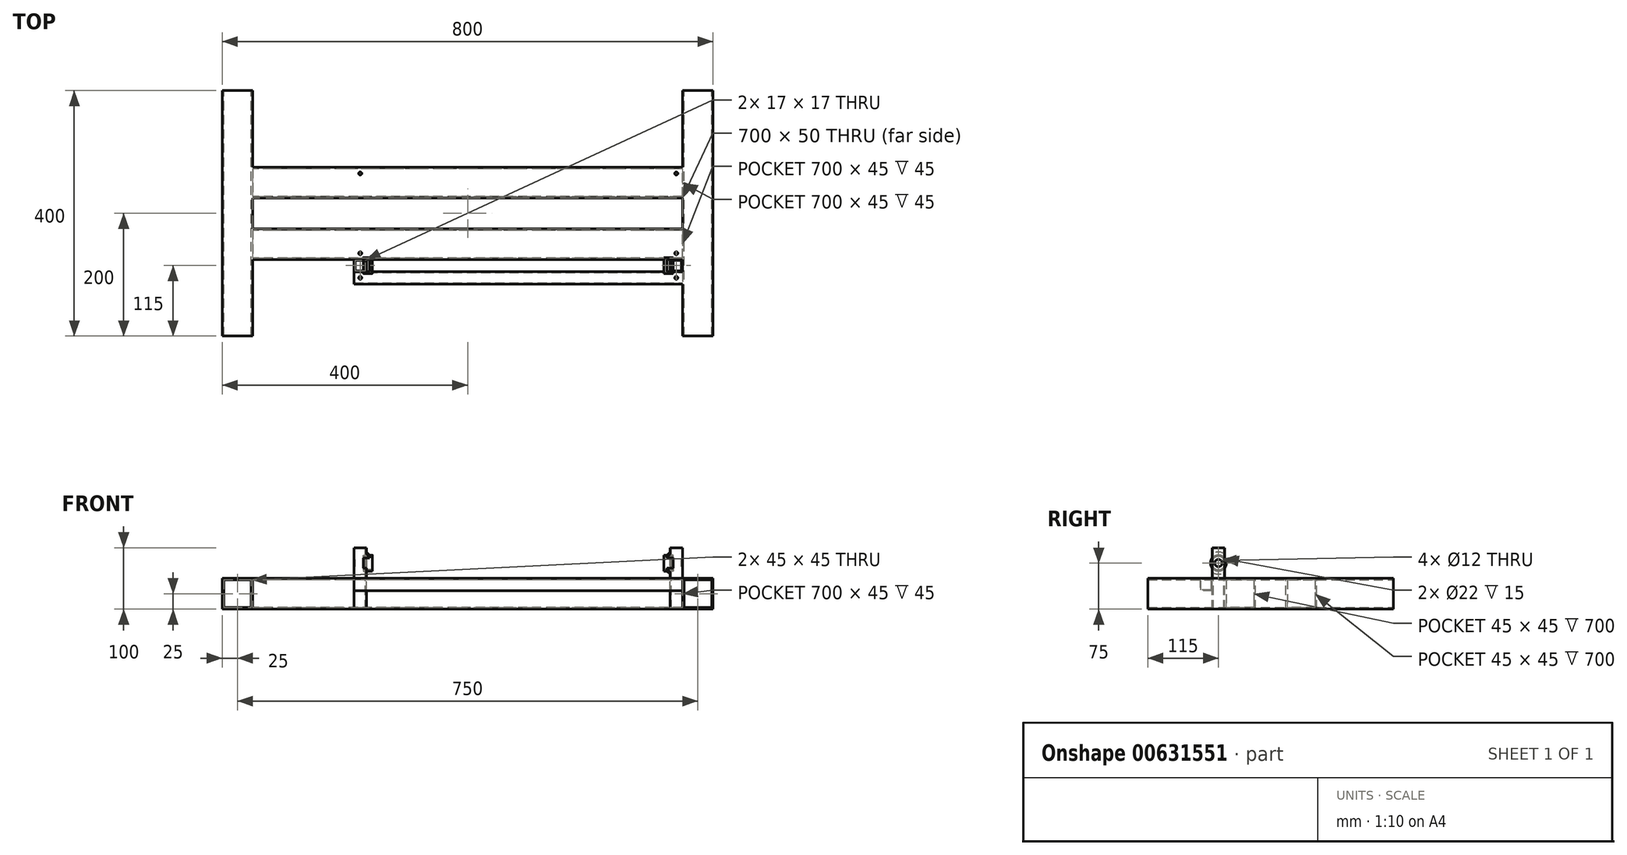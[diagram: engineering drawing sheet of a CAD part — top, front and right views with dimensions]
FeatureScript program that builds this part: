
annotation { "Feature Type Name" : "Feature", "Feature Type Description" : "" }
export const myFeature = defineFeature(function(context is Context, id is Id, definition is map)
    precondition{}
    {
        {
            var Q0;
            Q0=qCreatedBy(makeId("Front.planeOp"),FACE);
            var sketch = newSketch(context, id + "F0", { "sketchPlane" : qUnion([Q0])});
            skLineSegment(sketch, "E0.bottom", {"start": v(-400, -25) * mm, "end": v(-350, -25) * mm});
            skLineSegment(sketch, "E0.top", {"start": v(-400, 25) * mm, "end": v(-350, 25) * mm});
            skLineSegment(sketch, "E0.left", {"start": v(-400, -25) * mm, "end": v(-400, 25) * mm});
            skLineSegment(sketch, "E0.right", {"start": v(-350, -25) * mm, "end": v(-350, 25) * mm});
            skPoint(sketch, "E0.middle", {"position": v(-375, 0) * mm});
            skLineSegment(sketch, "E1.bottom", {"start": v(350, -25) * mm, "end": v(400, -25) * mm});
            skLineSegment(sketch, "E1.top", {"start": v(350, 25) * mm, "end": v(400, 25) * mm});
            skLineSegment(sketch, "E1.left", {"start": v(350, -25) * mm, "end": v(350, 25) * mm});
            skLineSegment(sketch, "E1.right", {"start": v(400, -25) * mm, "end": v(400, 25) * mm});
            skPoint(sketch, "E1.middle", {"position": v(375, 0) * mm});
            skLineSegment(sketch, "E2.bottom", {"start": v(-397.5, -22.5) * mm, "end": v(-352.5, -22.5) * mm});
            skLineSegment(sketch, "E2.top", {"start": v(-397.5, 22.5) * mm, "end": v(-352.5, 22.5) * mm});
            skLineSegment(sketch, "E2.left", {"start": v(-397.5, -22.5) * mm, "end": v(-397.5, 22.5) * mm});
            skLineSegment(sketch, "E2.right", {"start": v(-352.5, -22.5) * mm, "end": v(-352.5, 22.5) * mm});
            skLineSegment(sketch, "E3.bottom", {"start": v(352.5, -22.5) * mm, "end": v(397.5, -22.5) * mm});
            skLineSegment(sketch, "E3.top", {"start": v(352.5, 22.5) * mm, "end": v(397.5, 22.5) * mm});
            skLineSegment(sketch, "E3.left", {"start": v(352.5, -22.5) * mm, "end": v(352.5, 22.5) * mm});
            skLineSegment(sketch, "E3.right", {"start": v(397.5, -22.5) * mm, "end": v(397.5, 22.5) * mm});
            skSolve(sketch);
        }
        {
            var Q0;
            Q0 = qSketchRegion(id + "F0", true);
            extrude(context, id + "F1", {"entities" : qUnion([Q0]), "endBound" : BoundingType.SYMMETRIC, "depth" : 400 * mm, "offsetDistance" : 25 * mm});
        }
        {
            var Q0;
            Q0=makeQuery(id+"F1.opExtrude","SWEPT_FACE",FACE,{"disambiguationData":[OSD([sQuery(id+"F0.wireOp",EDGE,"E0.right")])]});
            var sketch = newSketch(context, id + "F2", { "sketchPlane" : qUnion([Q0])});
            skPoint(sketch, "E4.middle", {"position": v(0, 0) * mm});
            skLineSegment(sketch, "E5.bottom", {"start": v(75, -25) * mm, "end": v(25, -25) * mm});
            skLineSegment(sketch, "E5.top", {"start": v(75, 25) * mm, "end": v(25, 25) * mm});
            skLineSegment(sketch, "E5.left", {"start": v(75, -25) * mm, "end": v(75, 25) * mm});
            skLineSegment(sketch, "E5.right", {"start": v(25, -25) * mm, "end": v(25, 25) * mm});
            skPoint(sketch, "E5.middle", {"position": v(50, 0) * mm});
            skLineSegment(sketch, "E6.bottom", {"start": v(-25, -25) * mm, "end": v(-75, -25) * mm});
            skLineSegment(sketch, "E6.top", {"start": v(-25, 25) * mm, "end": v(-75, 25) * mm});
            skLineSegment(sketch, "E6.left", {"start": v(-25, -25) * mm, "end": v(-25, 25) * mm});
            skLineSegment(sketch, "E6.right", {"start": v(-75, -25) * mm, "end": v(-75, 25) * mm});
            skPoint(sketch, "E6.middle", {"position": v(-50, 0) * mm});
            skLineSegment(sketch, "E7.bottom", {"start": v(72.5, 22.5) * mm, "end": v(27.5, 22.5) * mm});
            skLineSegment(sketch, "E7.top", {"start": v(72.5, -22.5) * mm, "end": v(27.5, -22.5) * mm});
            skLineSegment(sketch, "E7.left", {"start": v(72.5, 22.5) * mm, "end": v(72.5, -22.5) * mm});
            skLineSegment(sketch, "E7.right", {"start": v(27.5, 22.5) * mm, "end": v(27.5, -22.5) * mm});
            skLineSegment(sketch, "E8.bottom", {"start": v(-27.5, 22.5) * mm, "end": v(-72.5, 22.5) * mm});
            skLineSegment(sketch, "E8.top", {"start": v(-27.5, -22.5) * mm, "end": v(-72.5, -22.5) * mm});
            skLineSegment(sketch, "E8.left", {"start": v(-27.5, 22.5) * mm, "end": v(-27.5, -22.5) * mm});
            skLineSegment(sketch, "E8.right", {"start": v(-72.5, 22.5) * mm, "end": v(-72.5, -22.5) * mm});
            skSolve(sketch);
        }
        {
            var Q0;
            Q0 = qSketchRegion(id + "F2", true);
            extrude(context, id + "F3", {"entities" : qUnion([Q0]), "operationType" : NewBodyOperationType.ADD, "endBound" : BoundingType.UP_TO_NEXT, "depth" : 25 * mm, "offsetDistance" : 25 * mm});
        }
        {
            var Q0;
            Q0=makeQuery(id+"F3.boolean.opBoolean","MERGE",FACE,{"derivedFrom":[makeQuery(id+"F1.opExtrude","SWEPT_FACE",FACE,{"disambiguationData":[OSD([sQuery(id+"F0.wireOp",EDGE,"E0.top")])]}),makeQuery(id+"F1.opExtrude","SWEPT_FACE",FACE,{"disambiguationData":[OSD([sQuery(id+"F0.wireOp",EDGE,"E1.top")])]}),makeQuery(id+"F3.opExtrude","SWEPT_FACE",FACE,{"disambiguationData":[OSD([sQuery(id+"F2.wireOp",EDGE,"E5.top")])]}),makeQuery(id+"F3.opExtrude","SWEPT_FACE",FACE,{"disambiguationData":[OSD([sQuery(id+"F2.wireOp",EDGE,"E6.top")])]})]});
            var sketch = newSketch(context, id + "F4", { "sketchPlane" : qUnion([Q0])});
            skLineSegment(sketch, "E9.bottom", {"start": v(350, -75) * mm, "end": v(330, -75) * mm});
            skLineSegment(sketch, "E9.top", {"start": v(350, -95) * mm, "end": v(330, -95) * mm});
            skLineSegment(sketch, "E9.left", {"start": v(350, -75) * mm, "end": v(350, -95) * mm});
            skLineSegment(sketch, "E9.right", {"start": v(330, -75) * mm, "end": v(330, -95) * mm});
            skLineSegment(sketch, "E10.bottom", {"start": v(-165, -75) * mm, "end": v(-185, -75) * mm});
            skLineSegment(sketch, "E10.top", {"start": v(-165, -95) * mm, "end": v(-185, -95) * mm});
            skLineSegment(sketch, "E10.left", {"start": v(-165, -75) * mm, "end": v(-165, -95) * mm});
            skLineSegment(sketch, "E10.right", {"start": v(-185, -75) * mm, "end": v(-185, -95) * mm});
            skLineSegment(sketch, "E11.bottom", {"start": v(-183.5, -93.5) * mm, "end": v(-166.5, -93.5) * mm});
            skLineSegment(sketch, "E11.top", {"start": v(-183.5, -76.5) * mm, "end": v(-166.5, -76.5) * mm});
            skLineSegment(sketch, "E11.left", {"start": v(-183.5, -93.5) * mm, "end": v(-183.5, -76.5) * mm});
            skLineSegment(sketch, "E11.right", {"start": v(-166.5, -93.5) * mm, "end": v(-166.5, -76.5) * mm});
            skPoint(sketch, "E11.middle", {"position": v(-175, -85) * mm});
            skPoint(sketch, "E11.middle.positionSnap0", {"position": v(-165, -85) * mm});
            skPoint(sketch, "E11.middle.positionSnap1", {"position": v(-175, -95) * mm});
            skPoint(sketch, "E11.centerSnap0", {"position": v(-165, -85) * mm});
            skPoint(sketch, "E11.centerSnap1", {"position": v(-175, -95) * mm});
            skLineSegment(sketch, "E12.bottom", {"start": v(331.5, -93.5) * mm, "end": v(348.5, -93.5) * mm});
            skLineSegment(sketch, "E12.top", {"start": v(331.5, -76.5) * mm, "end": v(348.5, -76.5) * mm});
            skLineSegment(sketch, "E12.left", {"start": v(331.5, -93.5) * mm, "end": v(331.5, -76.5) * mm});
            skLineSegment(sketch, "E12.right", {"start": v(348.5, -93.5) * mm, "end": v(348.5, -76.5) * mm});
            skPoint(sketch, "E12.middle", {"position": v(340, -85) * mm});
            skPoint(sketch, "E12.middle.positionSnap0", {"position": v(330, -85) * mm});
            skPoint(sketch, "E12.middle.positionSnap1", {"position": v(340, -75) * mm});
            skPoint(sketch, "E12.centerSnap0", {"position": v(330, -85) * mm});
            skPoint(sketch, "E12.centerSnap1", {"position": v(340, -75) * mm});
            skSolve(sketch);
        }
        {
            var Q0;
            Q0 = qSketchRegion(id + "F4", true);
            extrude(context, id + "F5", {"entities" : qUnion([Q0]), "operationType" : NewBodyOperationType.ADD, "oppositeDirection" : true, "depth" : 50 * mm, "offsetDistance" : 25 * mm});
        }
        {
            var Q0;
            Q0 = qSketchRegion(id + "F4", true);
            extrude(context, id + "F6", {"entities" : qUnion([Q0]), "operationType" : NewBodyOperationType.ADD, "depth" : 50 * mm, "offsetDistance" : 25 * mm});
        }
        {
            var Q0;
            {var subQ1=sQuery(id+"F0.wireOp",EDGE,"E1.left");Q0=makeQuery(id+"F3.boolean.opBoolean","SPLIT",FACE,{"disambiguationData":[TD([makeQuery(id+"F3.opExtrude","SWEPT_FACE",FACE,{"disambiguationData":[OSD([sQuery(id+"F2.wireOp",EDGE,"E6.right")])]})])],"derivedFrom":makeQuery(id+"F1.opExtrude","SWEPT_FACE",FACE,{"disambiguationData":[OSD([subQ1])]})});}
            var sketch = newSketch(context, id + "F7", { "sketchPlane" : qUnion([Q0])});
            skLineSegment(sketch, "E13.bottom", {"start": v(95, 25) * mm, "end": v(115, 25) * mm});
            skLineSegment(sketch, "E13.top", {"start": v(95, 5) * mm, "end": v(115, 5) * mm});
            skLineSegment(sketch, "E13.left", {"start": v(95, 25) * mm, "end": v(95, 5) * mm});
            skLineSegment(sketch, "E13.right", {"start": v(115, 25) * mm, "end": v(115, 5) * mm});
            skPoint(sketch, "E13.middle", {"position": v(105, 15) * mm});
            skLineSegment(sketch, "E14.bottom", {"start": v(96.5, 6.5) * mm, "end": v(113.5, 6.5) * mm});
            skLineSegment(sketch, "E14.top", {"start": v(96.5, 23.5) * mm, "end": v(113.5, 23.5) * mm});
            skLineSegment(sketch, "E14.left", {"start": v(96.5, 6.5) * mm, "end": v(96.5, 23.5) * mm});
            skLineSegment(sketch, "E14.right", {"start": v(113.5, 6.5) * mm, "end": v(113.5, 23.5) * mm});
            skSolve(sketch);
        }
        {
            var Q0;
            Q0 = qSketchRegion(id + "F7", true);
            extrude(context, id + "F8", {"entities" : qUnion([Q0]), "operationType" : NewBodyOperationType.ADD, "depth" : 535 * mm, "offsetDistance" : 25 * mm});
        }
        {
            var Q0;
            Q0=makeQuery(id+"F6.opExtrude","SWEPT_FACE",FACE,{"disambiguationData":[OSD([sQuery(id+"F4.wireOp",EDGE,"E9.left")])]});
            var sketch = newSketch(context, id + "F9", { "sketchPlane" : qUnion([Q0])});
            skCircle(sketch, "E15", {"center": v(-85, 50) * mm, "radius": 6 * mm});
            skPoint(sketch, "E15.centerSnap0", {"position": v(-85, 75) * mm});
            skSolve(sketch);
        }
        {
            var Q0;
            Q0 = qSketchRegion(id + "F9", true);
            extrude(context, id + "F10", {"entities" : qUnion([Q0]), "operationType" : NewBodyOperationType.REMOVE, "endBound" : BoundingType.THROUGH_ALL, "oppositeDirection" : true, "depth" : 242 * mm, "offsetDistance" : 25 * mm});
        }
        {
            var Q0;
            {var subQ0=sQuery(id+"F4.wireOp",EDGE,"E9.right");Q0=makeQuery(id+"F6.boolean.opBoolean","MERGE",FACE,{"derivedFrom":[makeQuery(id+"F5.opExtrude","SWEPT_FACE",FACE,{"disambiguationData":[OSD([subQ0])]}),makeQuery(id+"F6.opExtrude","SWEPT_FACE",FACE,{"disambiguationData":[OSD([subQ0])]})]});}
            var sketch = newSketch(context, id + "F11", { "sketchPlane" : qUnion([Q0])});
            skCircle(sketch, "E16", {"center": v(85, 50) * mm, "radius": 11 * mm});
            skCircle(sketch, "E17", {"center": v(85, 50) * mm, "radius": 13 * mm});
            skSolve(sketch);
        }
        {
            var Q0;
            Q0 = qSketchRegion(id + "F11", true);
            extrude(context, id + "F12", {"entities" : qUnion([Q0]), "operationType" : NewBodyOperationType.ADD, "depth" : 10 * mm, "offsetDistance" : 25 * mm});
        }
        {
            var Q0;
            Q0 = qSketchRegion(id + "F11", true);
            extrude(context, id + "F13", {"entities" : qUnion([Q0]), "operationType" : NewBodyOperationType.ADD, "oppositeDirection" : true, "depth" : 5 * mm, "offsetDistance" : 25 * mm});
        }
        {
            var Q0;
            {var subQ0=sQuery(id+"F4.wireOp",EDGE,"E10.left");Q0=makeQuery(id+"F6.boolean.opBoolean","MERGE",FACE,{"derivedFrom":[makeQuery(id+"F5.opExtrude","SWEPT_FACE",FACE,{"disambiguationData":[OSD([subQ0])]}),makeQuery(id+"F6.opExtrude","SWEPT_FACE",FACE,{"disambiguationData":[OSD([subQ0])]})]});}
            var sketch = newSketch(context, id + "F14", { "sketchPlane" : qUnion([Q0])});
            skCircle(sketch, "E18", {"center": v(-85, 50) * mm, "radius": 11 * mm});
            skCircle(sketch, "E19", {"center": v(-85, 50) * mm, "radius": 13 * mm});
            skSolve(sketch);
        }
        {
            var Q0;
            Q0 = qSketchRegion(id + "F14", true);
            extrude(context, id + "F15", {"entities" : qUnion([Q0]), "operationType" : NewBodyOperationType.ADD, "depth" : 10 * mm, "offsetDistance" : 25 * mm});
        }
        {
            var Q0;
            Q0 = qSketchRegion(id + "F14", true);
            extrude(context, id + "F16", {"entities" : qUnion([Q0]), "operationType" : NewBodyOperationType.ADD, "oppositeDirection" : true, "depth" : 5 * mm, "offsetDistance" : 25 * mm});
        }
        {
            var Q0;
            {var subQ0=sQuery(id+"F4.wireOp",EDGE,"E10.left");var subQ1=sQuery(id+"F14.wireOp",EDGE,"E19");Q0=makeQuery(id+"F15.boolean.opBoolean","SPLIT",EDGE,{"disambiguationData":[topologyDisambiguationEdgeConnected([makeQuery(id+"F5.opExtrude","SWEPT_FACE",FACE,{"disambiguationData":[OSD([subQ0])]}),makeQuery(id+"F6.opExtrude","SWEPT_FACE",FACE,{"disambiguationData":[OSD([subQ0])]}),makeQuery(id+"F15.opExtrude","SWEPT_FACE",FACE,{"disambiguationData":[OSD([subQ1])]})]),OD(1.0)],"derivedFrom":makeQuery(id+"F15.opExtrude","CAP_EDGE",EDGE,{"disambiguationData":[OSD([subQ1])],"isStart":true})});}
            var Q1;
            {var subQ0=sQuery(id+"F4.wireOp",EDGE,"E10.left");var subQ1=sQuery(id+"F14.wireOp",EDGE,"E19");Q1=makeQuery(id+"F15.boolean.opBoolean","SPLIT",EDGE,{"disambiguationData":[topologyDisambiguationEdgeConnected([makeQuery(id+"F5.opExtrude","SWEPT_FACE",FACE,{"disambiguationData":[OSD([subQ0])]}),makeQuery(id+"F6.opExtrude","SWEPT_FACE",FACE,{"disambiguationData":[OSD([subQ0])]}),makeQuery(id+"F15.opExtrude","SWEPT_FACE",FACE,{"disambiguationData":[OSD([subQ1])]})]),OD(0.0)],"derivedFrom":makeQuery(id+"F15.opExtrude","CAP_EDGE",EDGE,{"disambiguationData":[OSD([subQ1])],"isStart":true})});}
            var Q2;
            {var subQ0=sQuery(id+"F4.wireOp",EDGE,"E9.right");var subQ1=sQuery(id+"F11.wireOp",EDGE,"E17");Q2=makeQuery(id+"F12.boolean.opBoolean","SPLIT",EDGE,{"disambiguationData":[topologyDisambiguationEdgeConnected([makeQuery(id+"F5.opExtrude","SWEPT_FACE",FACE,{"disambiguationData":[OSD([subQ0])]}),makeQuery(id+"F6.opExtrude","SWEPT_FACE",FACE,{"disambiguationData":[OSD([subQ0])]}),makeQuery(id+"F12.opExtrude","SWEPT_FACE",FACE,{"disambiguationData":[OSD([subQ1])]})]),OD(1.0)],"derivedFrom":makeQuery(id+"F12.opExtrude","CAP_EDGE",EDGE,{"disambiguationData":[OSD([subQ1])],"isStart":true})});}
            var Q3;
            {var subQ0=sQuery(id+"F4.wireOp",EDGE,"E9.right");var subQ1=sQuery(id+"F11.wireOp",EDGE,"E17");Q3=makeQuery(id+"F12.boolean.opBoolean","SPLIT",EDGE,{"disambiguationData":[topologyDisambiguationEdgeConnected([makeQuery(id+"F5.opExtrude","SWEPT_FACE",FACE,{"disambiguationData":[OSD([subQ0])]}),makeQuery(id+"F6.opExtrude","SWEPT_FACE",FACE,{"disambiguationData":[OSD([subQ0])]}),makeQuery(id+"F12.opExtrude","SWEPT_FACE",FACE,{"disambiguationData":[OSD([subQ1])]})]),OD(0.0)],"derivedFrom":makeQuery(id+"F12.opExtrude","CAP_EDGE",EDGE,{"disambiguationData":[OSD([subQ1])],"isStart":true})});}
            chamfer(context, id + "F17", {"entities" : qUnion([Q0, Q1, Q2, Q3]), "width" : 5 * mm, "tangentPropagation" : true});
        }
        {
            var Q0;
            Q0=makeQuery(id+"F8.boolean.opBoolean","MERGE",FACE,{"derivedFrom":[makeQuery(id+"F5.boolean.opBoolean","MERGE",FACE,{"derivedFrom":[makeQuery(id+"F3.boolean.opBoolean","MERGE",FACE,{"derivedFrom":[makeQuery(id+"F1.opExtrude","SWEPT_FACE",FACE,{"disambiguationData":[OSD([sQuery(id+"F0.wireOp",EDGE,"E0.top")])]}),makeQuery(id+"F1.opExtrude","SWEPT_FACE",FACE,{"disambiguationData":[OSD([sQuery(id+"F0.wireOp",EDGE,"E1.top")])]}),makeQuery(id+"F3.opExtrude","SWEPT_FACE",FACE,{"disambiguationData":[OSD([sQuery(id+"F2.wireOp",EDGE,"E5.top")])]}),makeQuery(id+"F3.opExtrude","SWEPT_FACE",FACE,{"disambiguationData":[OSD([sQuery(id+"F2.wireOp",EDGE,"E6.top")])]})]}),makeQuery(id+"F5.opExtrude","CAP_FACE",FACE,{"disambiguationData":[OSD([sQuery(id+"F4.wireOp",EDGE,"E9.bottom"),sQuery(id+"F4.wireOp",EDGE,"E9.top"),sQuery(id+"F4.wireOp",EDGE,"E9.left"),sQuery(id+"F4.wireOp",EDGE,"E9.right"),sQuery(id+"F4.wireOp",EDGE,"E12.bottom"),sQuery(id+"F4.wireOp",EDGE,"E12.top"),sQuery(id+"F4.wireOp",EDGE,"E12.left"),sQuery(id+"F4.wireOp",EDGE,"E12.right")])],"isStart":true}),makeQuery(id+"F5.opExtrude","CAP_FACE",FACE,{"disambiguationData":[OSD([sQuery(id+"F4.wireOp",EDGE,"E10.bottom"),sQuery(id+"F4.wireOp",EDGE,"E10.top"),sQuery(id+"F4.wireOp",EDGE,"E10.left"),sQuery(id+"F4.wireOp",EDGE,"E10.right"),sQuery(id+"F4.wireOp",EDGE,"E11.bottom"),sQuery(id+"F4.wireOp",EDGE,"E11.top"),sQuery(id+"F4.wireOp",EDGE,"E11.left"),sQuery(id+"F4.wireOp",EDGE,"E11.right")])],"isStart":true})]}),makeQuery(id+"F8.opExtrude","SWEPT_FACE",FACE,{"disambiguationData":[OSD([sQuery(id+"F7.wireOp",EDGE,"E13.bottom")])]})]});
            var sketch = newSketch(context, id + "F18", { "sketchPlane" : qUnion([Q0])});
            skCircle(sketch, "E20", {"center": v(-175, -65) * mm, "radius": 2.5 * mm});
            skCircle(sketch, "E21", {"center": v(-175, 65) * mm, "radius": 2.5 * mm});
            skCircle(sketch, "E22", {"center": v(-175, -105) * mm, "radius": 2.5 * mm});
            skCircle(sketch, "E23", {"center": v(340, -105) * mm, "radius": 2.5 * mm});
            skCircle(sketch, "E24", {"center": v(340, -65) * mm, "radius": 2.5 * mm});
            skCircle(sketch, "E25", {"center": v(340, 65) * mm, "radius": 2.5 * mm});
            skSolve(sketch);
        }
        {
            var Q0;
            Q0 = qSketchRegion(id + "F18", true);
            extrude(context, id + "F19", {"entities" : qUnion([Q0]), "operationType" : NewBodyOperationType.REMOVE, "oppositeDirection" : true, "depth" : 10 * mm, "offsetDistance" : 25 * mm});
        }
    });
